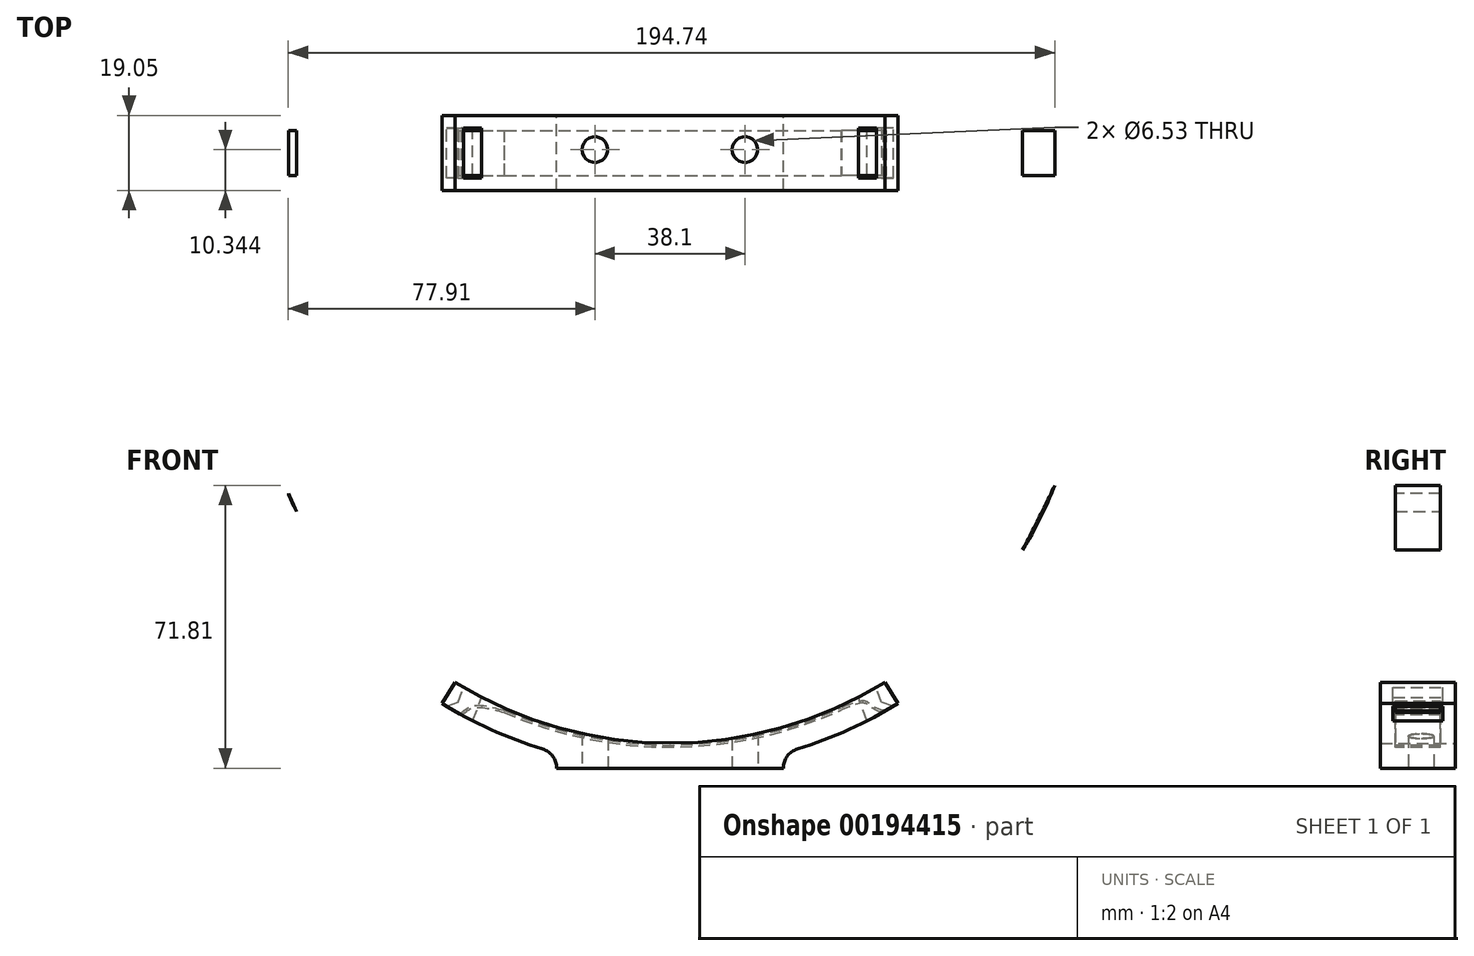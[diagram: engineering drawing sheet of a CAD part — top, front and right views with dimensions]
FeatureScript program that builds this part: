
annotation { "Feature Type Name" : "Feature", "Feature Type Description" : "" }
export const myFeature = defineFeature(function(context is Context, id is Id, definition is map)
    precondition{}
    {
        {
            var Q0;
            Q0=qCreatedBy(makeId("Front.planeOp"),FACE);
            var sketch = newSketch(context, id + "F0", { "sketchPlane" : qUnion([Q0])});
            skLineSegment(sketch, "E0", {"start": v(3.37, -3.8) * mm, "end": v(3.37, -18.65) * mm});
            skLineSegment(sketch, "E1", {"start": v(3.37, -3.8) * mm, "end": v(28.77, -3.8) * mm});
            skLineSegment(sketch, "E2", {"start": v(28.77, -3.8) * mm, "end": v(28.77, 0.95) * mm});
            skLineSegment(sketch, "E3", {"start": v(28.77, 0.95) * mm, "end": v(0, 0.95) * mm});
            skLineSegment(sketch, "E4", {"start": v(0, 0) * mm, "end": v(0, -19.34) * mm});
            skLineSegment(sketch, "E5.MirrorCS", {"start": v(-3.37, -3.8) * mm, "end": v(-28.77, -3.81) * mm});
            skLineSegment(sketch, "E6.MirrorCS", {"start": v(-28.77, -3.81) * mm, "end": v(-28.77, 0.95) * mm});
            skLineSegment(sketch, "E7.MirrorCS", {"start": v(-28.77, 0.95) * mm, "end": v(0, 0.95) * mm});
            skLineSegment(sketch, "E8.MirrorCS", {"start": v(-3.37, -3.8) * mm, "end": v(-3.37, -18.65) * mm});
            skPoint(sketch, "E9.MirrorCS.start.orphan", {"position": v(0, 0) * mm});
            skLineSegment(sketch, "E10", {"start": v(0, 7.3) * mm, "end": v(0, 111.44) * mm});
            skArc(sketch, "E11", {"start": v(-54.63, 22.78) * mm, "mid": v(0, 7.3) * mm, "end": v(54.63, 22.78) * mm});
            skArc(sketch, "E12", {"start": v(28.77, 4.76) * mm, "mid": v(43.82, 10.01) * mm, "end": v(57.96, 17.38) * mm});
            skLineSegment(sketch, "E13", {"start": v(-28.77, 0.95) * mm, "end": v(-28.77, 4.76) * mm});
            skLineSegment(sketch, "E14", {"start": v(28.77, 0.95) * mm, "end": v(28.77, 4.76) * mm});
            skLineSegment(sketch, "E15", {"start": v(0, 111.44) * mm, "end": v(-57.96, 17.38) * mm});
            skLineSegment(sketch, "E16.MirrorCS", {"start": v(0, 111.44) * mm, "end": v(57.96, 17.38) * mm});
            skArc(sketch, "E17.trimOffspring", {"start": v(-57.96, 17.38) * mm, "mid": v(-43.82, 10.01) * mm, "end": v(-28.77, 4.76) * mm});
            skSolve(sketch);
        }
        {
            var Q0;
            Q0=makeQuery(id+"F0.imprint","IMPRINT",FACE,{"disambiguationData":[TD([[makeQuery(id+"F0.imprint","IMPRINT",EDGE,{"derivedFrom":sQuery(id+"F0.wireOp",EDGE,"E3")}),-1.0]])]});
            extrude(context, id + "F1", {"entities" : qUnion([Q0]), "depth" : 19.05 * mm});
        }
        {
            var Q0;
            Q0=makeQuery(id+"F1.opExtrude","SWEPT_FACE",FACE,{"disambiguationData":[OSD([sQuery(id+"F0.wireOp",EDGE,"E3"),sQuery(id+"F0.wireOp",EDGE,"E7.MirrorCS")])]});
            var sketch = newSketch(context, id + "F2", { "sketchPlane" : qUnion([Q0])});
            skPoint(sketch, "E18.endSnap0", {"position": v(28.77, 9.53) * mm});
            skPoint(sketch, "E19.endSnap0", {"position": v(0, 19.05) * mm});
            skLineSegment(sketch, "E20.MirrorCS", {"start": v(28.77, 0) * mm, "end": v(28.77, 9.53) * mm});
            skPoint(sketch, "E18.end.orphan", {"position": v(-16.07, 9.53) * mm});
            skPoint(sketch, "E21.end.orphan", {"position": v(-28.77, 9.53) * mm});
            skPoint(sketch, "E21.start.orphan", {"position": v(-28.77, 0) * mm});
            skPoint(sketch, "E22.MirrorCS.end.orphan", {"position": v(16.07, 9.53) * mm});
            skPoint(sketch, "E19.end.orphan", {"position": v(0, 8.7) * mm});
            skPoint(sketch, "E19.start.orphan", {"position": v(0, 19.05) * mm});
            skLineSegment(sketch, "E23", {"start": v(0, 8.7) * mm, "end": v(-19.05, 8.7) * mm});
            skLineSegment(sketch, "E24", {"start": v(0, 8.7) * mm, "end": v(0, 15.12) * mm});
            skLineSegment(sketch, "E25.MirrorCS", {"start": v(0, 8.7) * mm, "end": v(19.05, 8.7) * mm});
            skSolve(sketch);
        }
        {
            var Q0;
            Q0=sQuery(id+"F2.wireOp",VERTEX,"E23.end");
            var Q1;
            Q1=sQuery(id+"F2.wireOp",VERTEX,"E25.MirrorCS.end");
            var Q2;
            Q2=makeQuery(id+"F1.opExtrude","SWEPT_BODY",BODY,{"disambiguationData":[OSD([sQuery(id+"F0.wireOp",EDGE,"E3"),sQuery(id+"F0.wireOp",EDGE,"E7.MirrorCS"),sQuery(id+"F0.wireOp",EDGE,"E11"),sQuery(id+"F0.wireOp",EDGE,"E12"),sQuery(id+"F0.wireOp",EDGE,"E13"),sQuery(id+"F0.wireOp",EDGE,"E14"),sQuery(id+"F0.wireOp",EDGE,"E15"),sQuery(id+"F0.wireOp",EDGE,"E16.MirrorCS"),sQuery(id+"F0.wireOp",EDGE,"E17.trimOffspring")])]});
            hole(context, id + "F3", {"style" : HoleStyle.SIMPLE, "endStyle" : HoleEndStyle.BLIND, "standardTappedOrClearance" : lookupTablePath({ "standard" : "ANSI", "fit" : "Close", "size" : "1/4", "type" : "Clearance" }), "standardBlindInLast" : lookupTablePath({ "fit" : "Close", "standard" : "ANSI", "size" : "1/4", "type" : "Clearance" }), "holeDiameter" : 6.53 * mm, "holeDepth" : 101.6 * mm, "locations" : qUnion([Q0, Q1]), "scope" : qUnion([Q2])});
        }
        {
            var Q0;
            Q0=makeQuery(id+"F1.opExtrude","SWEPT_EDGE",EDGE,{"disambiguationData":[OSD([sQuery(id+"F0.wireOp",EDGE,"E11"),sQuery(id+"F0.wireOp",EDGE,"E15")])]});
            cPlane(context, id + "F4", {"entities" : qUnion([Q0]), "cplaneType" : CPlaneType.LINE_ANGLE, "offset" : 25.4 * mm, "angle" : 20 * degree, "width" : 152.4 * mm, "height" : 152.4 * mm});
        }
        {
            var Q0;
            Q0=makeQuery(id+"F1.opExtrude","SWEPT_EDGE",EDGE,{"disambiguationData":[OSD([sQuery(id+"F0.wireOp",EDGE,"E11"),sQuery(id+"F0.wireOp",EDGE,"E16.MirrorCS")])]});
            cPlane(context, id + "F5", {"entities" : qUnion([Q0]), "cplaneType" : CPlaneType.LINE_ANGLE, "offset" : 25.4 * mm, "angle" : 340 * degree, "width" : 152.4 * mm, "height" : 152.4 * mm});
        }
        {
            var Q0;
            Q0=qCreatedBy(id+"F4.planeOp",FACE);
            var sketch = newSketch(context, id + "F6", { "sketchPlane" : qUnion([Q0])});
            skLineSegment(sketch, "E26", {"start": v(-59.13, -19.05) * mm, "end": v(-59.13, -9.53) * mm});
            skLineSegment(sketch, "E27", {"start": v(-59.13, -9.53) * mm, "end": v(-54.05, -9.53) * mm});
            skLineSegment(sketch, "E28.bottom", {"start": v(-51.5, -15.88) * mm, "end": v(-56.59, -15.88) * mm});
            skLineSegment(sketch, "E28.top", {"start": v(-51.5, -3.18) * mm, "end": v(-56.59, -3.18) * mm});
            skLineSegment(sketch, "E28.left", {"start": v(-51.5, -15.88) * mm, "end": v(-51.5, -3.18) * mm});
            skLineSegment(sketch, "E28.right", {"start": v(-56.59, -15.88) * mm, "end": v(-56.59, -3.18) * mm});
            skPoint(sketch, "E28.middle", {"position": v(-54.05, -9.53) * mm});
            skSolve(sketch);
        }
        {
            var Q0;
            {var subQ0=sQuery(id+"F6.wireOp",EDGE,"E28.bottom");Q0=makeQuery(id+"F6.imprint","IMPRINT",FACE,{"disambiguationData":[TD([[makeQuery(id+"F6.imprint","IMPRINT",EDGE,{"derivedFrom":subQ0}),-1.0]])]});}
            extrude(context, id + "F7", {"entities" : qUnion([Q0]), "operationType" : NewBodyOperationType.REMOVE, "oppositeDirection" : true, "depth" : 25.4 * mm});
        }
        {
            var Q0;
            Q0=qCreatedBy(id+"F5.planeOp",FACE);
            var sketch = newSketch(context, id + "F8", { "sketchPlane" : qUnion([Q0])});
            skLineSegment(sketch, "E29", {"start": v(59.13, -19.05) * mm, "end": v(59.13, -9.53) * mm});
            skLineSegment(sketch, "E30", {"start": v(59.13, -9.53) * mm, "end": v(54.05, -9.53) * mm});
            skLineSegment(sketch, "E31.bottom", {"start": v(56.59, -3.18) * mm, "end": v(51.5, -3.18) * mm});
            skLineSegment(sketch, "E31.top", {"start": v(56.59, -15.88) * mm, "end": v(51.5, -15.88) * mm});
            skLineSegment(sketch, "E31.left", {"start": v(56.59, -3.18) * mm, "end": v(56.59, -15.88) * mm});
            skLineSegment(sketch, "E31.right", {"start": v(51.5, -3.18) * mm, "end": v(51.5, -15.88) * mm});
            skPoint(sketch, "E31.middle", {"position": v(54.05, -9.53) * mm});
            skSolve(sketch);
        }
        {
            var Q0;
            {var subQ0=sQuery(id+"F8.wireOp",EDGE,"E31.bottom");Q0=makeQuery(id+"F8.imprint","IMPRINT",FACE,{"disambiguationData":[TD([[makeQuery(id+"F8.imprint","IMPRINT",EDGE,{"derivedFrom":subQ0}),1.0]])]});}
            extrude(context, id + "F9", {"entities" : qUnion([Q0]), "operationType" : NewBodyOperationType.REMOVE, "oppositeDirection" : true, "depth" : 25.4 * mm});
        }
        {
            var Q0;
            Q0=makeQuery(id+"F7.boolean.opBoolean","INTERSECT",EDGE,{"derivedFrom":[makeQuery(id+"F1.opExtrude","SWEPT_FACE",FACE,{"disambiguationData":[OSD([sQuery(id+"F0.wireOp",EDGE,"E17.trimOffspring")])]}),makeQuery(id+"F7.opExtrude","SWEPT_FACE",FACE,{"disambiguationData":[OSD([sQuery(id+"F6.wireOp",EDGE,"E28.right")])]})]});
            var Q1;
            Q1=makeQuery(id+"F9.boolean.opBoolean","INTERSECT",EDGE,{"derivedFrom":[makeQuery(id+"F1.opExtrude","SWEPT_FACE",FACE,{"disambiguationData":[OSD([sQuery(id+"F0.wireOp",EDGE,"E12")])]}),makeQuery(id+"F9.opExtrude","SWEPT_FACE",FACE,{"disambiguationData":[OSD([sQuery(id+"F8.wireOp",EDGE,"E31.left")])]})]});
            chamfer(context, id + "F10", {"entities" : qUnion([Q0, Q1]), "width" : 2.03 * mm, "tangentPropagation" : true});
        }
        {
            var Q0;
            Q0=makeQuery(id+"F1.opExtrude","SWEPT_EDGE",EDGE,{"disambiguationData":[OSD([sQuery(id+"F0.wireOp",EDGE,"E12"),sQuery(id+"F0.wireOp",EDGE,"E14")])]});
            var Q1;
            Q1=makeQuery(id+"F1.opExtrude","SWEPT_EDGE",EDGE,{"disambiguationData":[OSD([sQuery(id+"F0.wireOp",EDGE,"E13"),sQuery(id+"F0.wireOp",EDGE,"E17.trimOffspring")])]});
            fillet(context, id + "F11", {"entities" : qUnion([Q0, Q1]), "radius" : 5.08 * mm, "tangentPropagation" : true, "allowEdgeOverflow" : false});
        }
        {
            var Q0;
            Q0=makeQuery(id+"F1.opExtrude","CAP_FACE",FACE,{"disambiguationData":[OSD([sQuery(id+"F0.wireOp",EDGE,"E3"),sQuery(id+"F0.wireOp",EDGE,"E7.MirrorCS"),sQuery(id+"F0.wireOp",EDGE,"E11"),sQuery(id+"F0.wireOp",EDGE,"E12"),sQuery(id+"F0.wireOp",EDGE,"E13"),sQuery(id+"F0.wireOp",EDGE,"E14"),sQuery(id+"F0.wireOp",EDGE,"E15"),sQuery(id+"F0.wireOp",EDGE,"E16.MirrorCS"),sQuery(id+"F0.wireOp",EDGE,"E17.trimOffspring")])],"isStart":false});
            var sketch = newSketch(context, id + "F12", { "sketchPlane" : qUnion([Q0])});
            skCircle(sketch, "E32", {"center": v(0, 111.44) * mm, "radius": 104.14 * mm});
            skLineSegment(sketch, "E33", {"start": v(0, 111.44) * mm, "end": v(0, 215.58) * mm});
            skLineSegment(sketch, "E34.0", {"start": v(-94.42, 66.33) * mm, "end": v(-94.42, 66.33) * mm});
            skArc(sketch, "E35.0", {"start": v(-42.16, 15.1) * mm, "mid": v(0.74, 6.29) * mm, "end": v(43.5, 15.7) * mm});
            skFitSpline(sketch, "E36", {"points": [v(-96.96, 70.73) * mm, v(-76.74, 34.37) * mm, v(-54.05, 14.36) * mm, v(-50.32, 16.18) * mm, v(-42.16, 15.1) * mm], "startDerivative": vector(42.9, -96.2) * mm, "endDerivative": vector(55.19, -15.23) * mm});
            skFitSpline(sketch, "E37.0", {"points": [v(-96.5, 70.94) * mm, v(-94.7, 66.93) * mm, v(-91.12, 58.94) * mm, v(-85.99, 49.04) * mm, v(-81.72, 42.18) * mm, v(-79.05, 38.3) * mm, v(-76.91, 35.39) * mm, v(-74.63, 32.5) * mm, v(-71.43, 28.7) * mm, v(-68.1, 25.12) * mm, v(-64.84, 21.94) * mm, v(-62.47, 19.82) * mm, v(-60.23, 18) * mm, v(-58.16, 16.54) * mm, v(-56.63, 15.66) * mm, v(-55.56, 15.2) * mm, v(-54.84, 14.97) * mm, v(-54.22, 14.86) * mm, v(-53.73, 14.87) * mm, v(-53.3, 14.98) * mm, v(-52.9, 15.16) * mm, v(-52.49, 15.41) * mm, v(-52.07, 15.72) * mm, v(-51.63, 16.04) * mm, v(-51.14, 16.37) * mm, v(-50.67, 16.6) * mm, v(-50.26, 16.74) * mm, v(-49.83, 16.85) * mm, v(-49.27, 16.93) * mm, v(-48.33, 16.96) * mm, v(-47.06, 16.84) * mm, v(-45.44, 16.51) * mm, v(-43.75, 16.08) * mm, v(-42.6, 15.76) * mm, v(-42.03, 15.6) * mm]});
            skArc(sketch, "E38", {"start": v(-42.03, 15.6) * mm, "mid": v(0.76, 6.8) * mm, "end": v(43.4, 16.22) * mm});
            skFitSpline(sketch, "E39", {"points": [v(97.78, 72.76) * mm, v(75.67, 33.06) * mm, v(56.74, 15.15) * mm, v(51.05, 16.46) * mm, v(49.3, 17.48) * mm, v(43.5, 15.7) * mm], "startDerivative": vector(-54.97, -112.48) * mm, "endDerivative": vector(-50.81, -20.22) * mm});
            skFitSpline(sketch, "E40.0", {"points": [v(97.32, 72.98) * mm, v(95.03, 68.3) * mm, v(90.44, 58.93) * mm, v(84.39, 47.64) * mm, v(79.18, 39.09) * mm, v(75.06, 32.96) * mm, v(70.68, 27.2) * mm, v(66.99, 23) * mm, v(64.1, 20.21) * mm, v(62.01, 18.44) * mm, v(60, 17.04) * mm, v(58.44, 16.22) * mm, v(57.28, 15.8) * mm, v(56.45, 15.6) * mm, v(55.66, 15.5) * mm, v(54.67, 15.51) * mm, v(53.53, 15.73) * mm, v(52.36, 16.21) * mm, v(51.58, 16.7) * mm, v(51.1, 17.06) * mm, v(50.77, 17.33) * mm, v(50.42, 17.6) * mm, v(50.02, 17.83) * mm, v(49.62, 17.95) * mm, v(49.26, 18) * mm, v(48.9, 18) * mm, v(48.4, 17.95) * mm, v(47.57, 17.77) * mm, v(46.42, 17.4) * mm, v(44.9, 16.82) * mm, v(43.85, 16.4) * mm, v(43.32, 16.18) * mm]});
            skFitSpline(sketch, "E41.trimOffspring", {"points": [v(97.32, 72.98) * mm, v(95.03, 68.3) * mm, v(90.44, 58.93) * mm, v(84.39, 47.64) * mm, v(79.18, 39.09) * mm, v(75.06, 32.96) * mm, v(70.68, 27.2) * mm, v(66.99, 23) * mm, v(64.1, 20.21) * mm, v(62.01, 18.44) * mm, v(60, 17.04) * mm, v(58.44, 16.22) * mm, v(57.28, 15.8) * mm, v(56.45, 15.6) * mm, v(55.66, 15.5) * mm, v(54.67, 15.51) * mm, v(53.53, 15.73) * mm, v(52.36, 16.21) * mm, v(51.58, 16.7) * mm, v(51.1, 17.06) * mm, v(50.77, 17.33) * mm, v(50.42, 17.6) * mm, v(50.02, 17.83) * mm, v(49.62, 17.95) * mm, v(49.26, 18) * mm, v(48.9, 18) * mm, v(48.4, 17.95) * mm, v(47.57, 17.77) * mm, v(46.42, 17.4) * mm, v(44.9, 16.82) * mm, v(43.85, 16.4) * mm, v(43.32, 16.18) * mm]});
            skArc(sketch, "E42.trimOffspring", {"start": v(89.59, 56.38) * mm, "mid": v(5.54, 216.45) * mm, "end": v(-94.89, 66.12) * mm});
            skArc(sketch, "E43.trimOffspring", {"start": v(89.11, 56.57) * mm, "mid": v(5.44, 215.95) * mm, "end": v(-94.32, 66.1) * mm});
            skLineSegment(sketch, "E44", {"start": v(43.4, 16.22) * mm, "end": v(47.93, 17.84) * mm});
            skSolve(sketch);
        }
        {
            var Q0;
            {var subQ4=sQuery(id+"F12.wireOp",EDGE,"E42.trimOffspring");Q0=makeQuery(id+"F12.imprint","IMPRINT",FACE,{"disambiguationData":[TD([[makeQuery(id+"F12.imprint","IMPRINT",EDGE,{"derivedFrom":subQ4}),1.0]])]});}
            var Q1;
            {var subQ5=sQuery(id+"F12.wireOp",EDGE,"E35.0");Q1=makeQuery(id+"F12.imprint","IMPRINT",FACE,{"disambiguationData":[TD([[makeQuery(id+"F12.imprint","IMPRINT",EDGE,{"derivedFrom":subQ5}),1.0]])]});}
            extrude(context, id + "F13", {"entities" : qUnion([Q0, Q1]), "oppositeDirection" : true, "depth" : 15.24 * mm, "hasSecondDirection" : true, "secondDirectionOppositeDirection" : true, "secondDirectionDepth" : 3.8 * mm});
        }
    });
